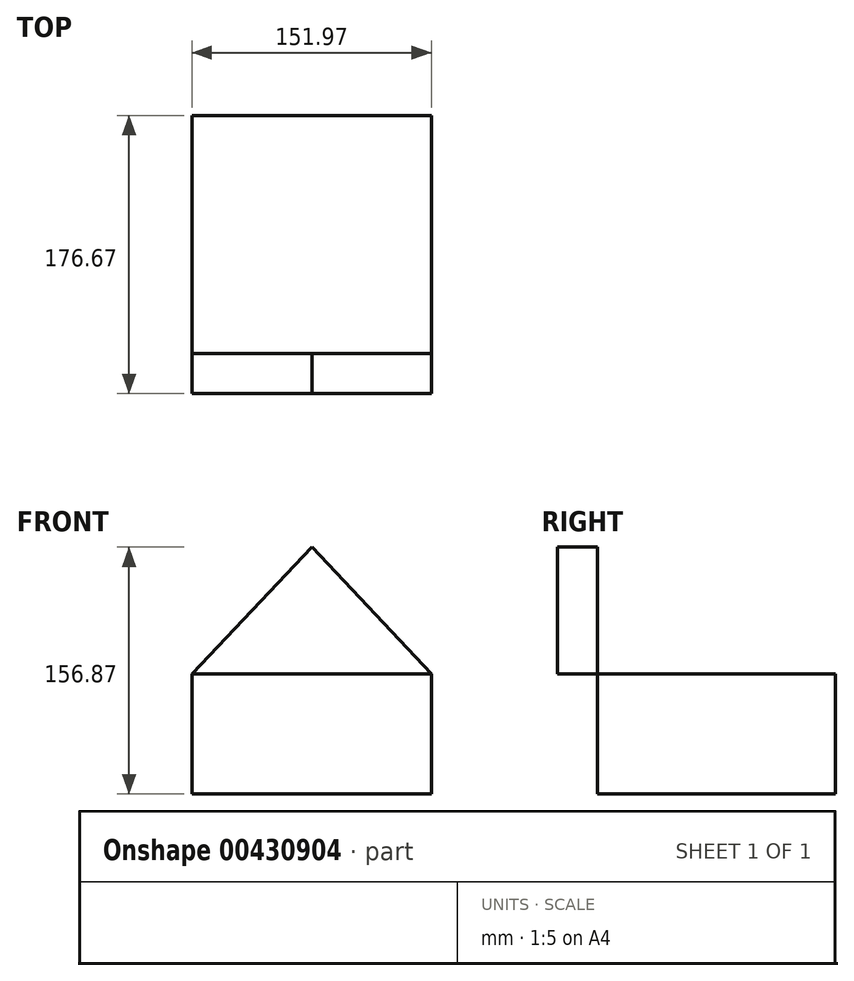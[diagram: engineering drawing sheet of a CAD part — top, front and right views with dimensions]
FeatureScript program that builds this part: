
annotation { "Feature Type Name" : "Feature", "Feature Type Description" : "" }
export const myFeature = defineFeature(function(context is Context, id is Id, definition is map)
    precondition{}
    {
        {
            var Q0;
            Q0=qCreatedBy(makeId("Top.planeOp"),FACE);
            var sketch = newSketch(context, id + "F0", { "sketchPlane" : qUnion([Q0])});
            skLineSegment(sketch, "E0.bottom", {"start": v(-76.1, 75.12) * mm, "end": v(75.87, 75.12) * mm});
            skLineSegment(sketch, "E0.top", {"start": v(-76.1, -76.15) * mm, "end": v(75.87, -76.15) * mm});
            skLineSegment(sketch, "E0.left", {"start": v(-76.1, 75.12) * mm, "end": v(-76.1, -76.15) * mm});
            skLineSegment(sketch, "E0.right", {"start": v(75.87, 75.12) * mm, "end": v(75.87, -76.15) * mm});
            skSolve(sketch);
        }
        {
            var Q0;
            Q0 = qSketchRegion(id + "F0", true);
            extrude(context, id + "F1", {"entities" : qUnion([Q0]), "depth" : 76.45 * mm});
        }
        {
            var Q0;
            Q0=makeQuery(id+"F1.opExtrude","SWEPT_FACE",FACE,{"disambiguationData":[OSD([sQuery(id+"F0.wireOp",EDGE,"E0.top")])]});
            var sketch = newSketch(context, id + "F2", { "sketchPlane" : qUnion([Q0])});
            skLineSegment(sketch, "E1", {"start": v(-76.1, 76.45) * mm, "end": v(0, 156.87) * mm});
            skLineSegment(sketch, "E2", {"start": v(0, 156.87) * mm, "end": v(75.87, 76.45) * mm});
            skLineSegment(sketch, "E3", {"start": v(75.87, 76.45) * mm, "end": v(-76.1, 76.45) * mm});
            skSolve(sketch);
        }
        {
            var Q0;
            Q0=makeQuery(id+"F2.imprint","IMPRINT",FACE,{"disambiguationData":[TD([[makeQuery(id+"F2.imprint","IMPRINT",EDGE,{"derivedFrom":sQuery(id+"F2.wireOp",EDGE,"E1")}),-1.0]])]});
            extrude(context, id + "F3", {"entities" : qUnion([Q0]), "depth" : 25.4 * mm});
        }
    });
